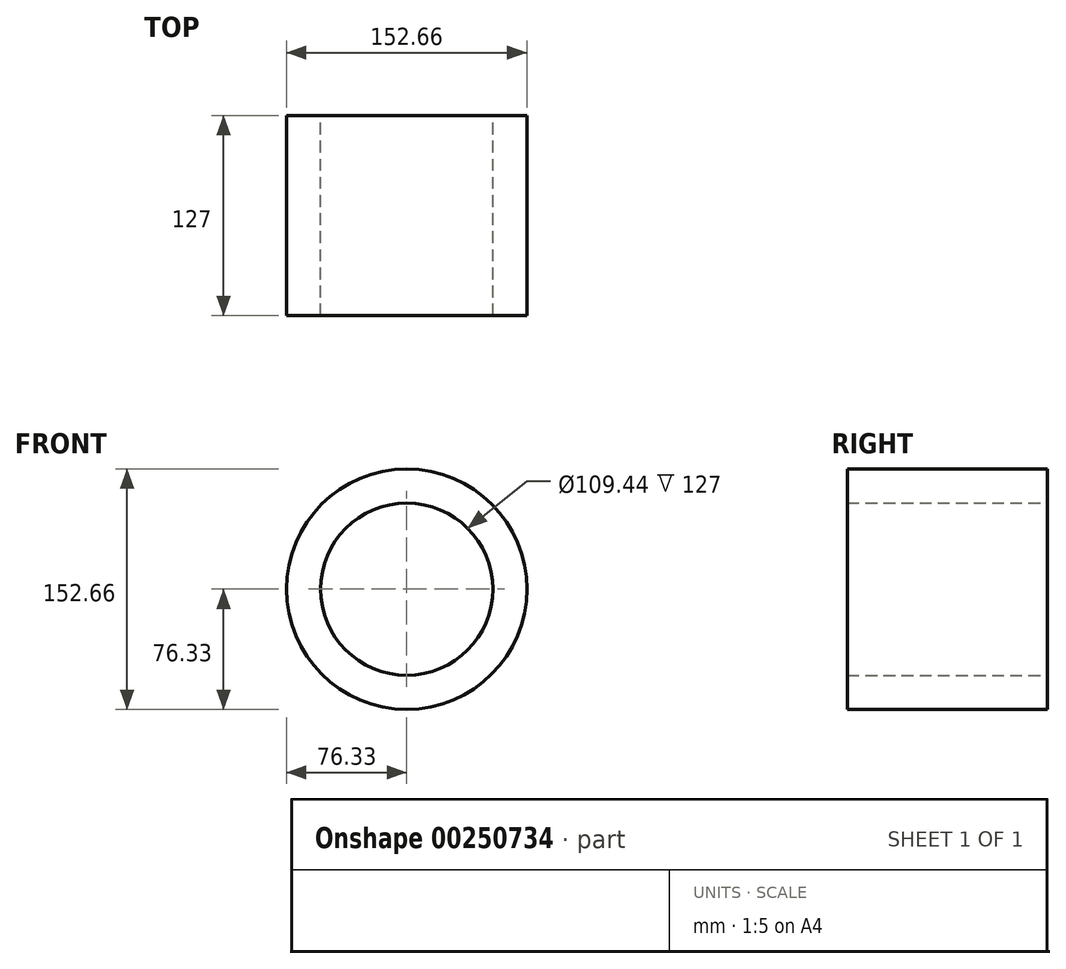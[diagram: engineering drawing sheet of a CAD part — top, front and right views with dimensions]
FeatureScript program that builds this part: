
annotation { "Feature Type Name" : "Feature", "Feature Type Description" : "" }
export const myFeature = defineFeature(function(context is Context, id is Id, definition is map)
    precondition{}
    {
        {
            var Q0;
            Q0=qCreatedBy(makeId("Front.planeOp"),FACE);
            var sketch = newSketch(context, id + "F0", { "sketchPlane" : qUnion([Q0])});
            skCircle(sketch, "E0", {"center": v(0, 0) * mm, "radius": 76.33 * mm});
            skSolve(sketch);
        }
        {
            var Q0;
            Q0=makeQuery(id+"F0.imprint","IMPRINT",FACE,{"disambiguationData":[TD([[makeQuery(id+"F0.imprint","IMPRINT",EDGE,{"derivedFrom":sQuery(id+"F0.wireOp",EDGE,"E0")}),1.0]])]});
            var sketch = newSketch(context, id + "F1", { "sketchPlane" : qUnion([Q0])});
            skCircle(sketch, "E1", {"center": v(0, 0) * mm, "radius": 54.72 * mm});
            skSolve(sketch);
        }
        {
            var Q0;
            Q0=makeQuery(id+"F1.imprint","IMPRINT",FACE,{"disambiguationData":[TD([[makeQuery(id+"F1.imprint","IMPRINT",EDGE,{"derivedFrom":sQuery(id+"F1.wireOp",EDGE,"E1")}),-1.0]])]});
            extrude(context, id + "F2", {"entities" : qUnion([Q0]), "depth" : 127 * mm});
        }
    });
